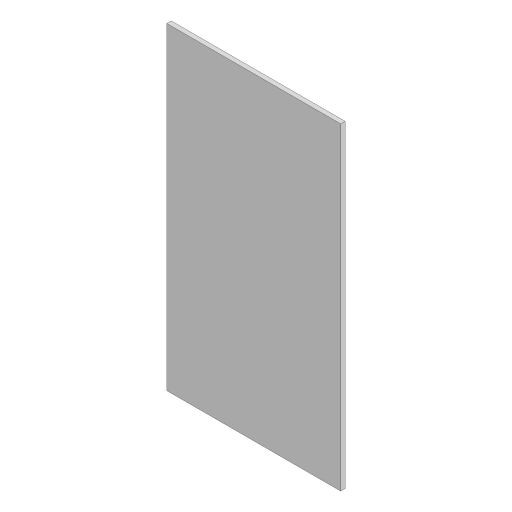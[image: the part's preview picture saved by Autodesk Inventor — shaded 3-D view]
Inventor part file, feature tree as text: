
AUTODESK INVENTOR PART (.ipt)
format: ipt  version: 2024 (Build 280153000, 153)  size: 81,920 bytes
history: native  units: in
note: dims shown in document units (in); Inventor stores cm internally (conversion verified against a paired STEP export)
features: extrude x1, sketch x1
ambient origin geometry x8: Origin, YZ Plane, XZ Plane, XY Plane, X Axis, Y Axis, Z Axis, Center Point
bodies: Solid1 (feature_tree)
feature tree (2):
  extrude  "Extrusion1"  Depth=93.8583in
  sketch  "Sketch1"  dims[d0=51.2992in d1=93.8583in d2=1.2992in d3=0.0in]
